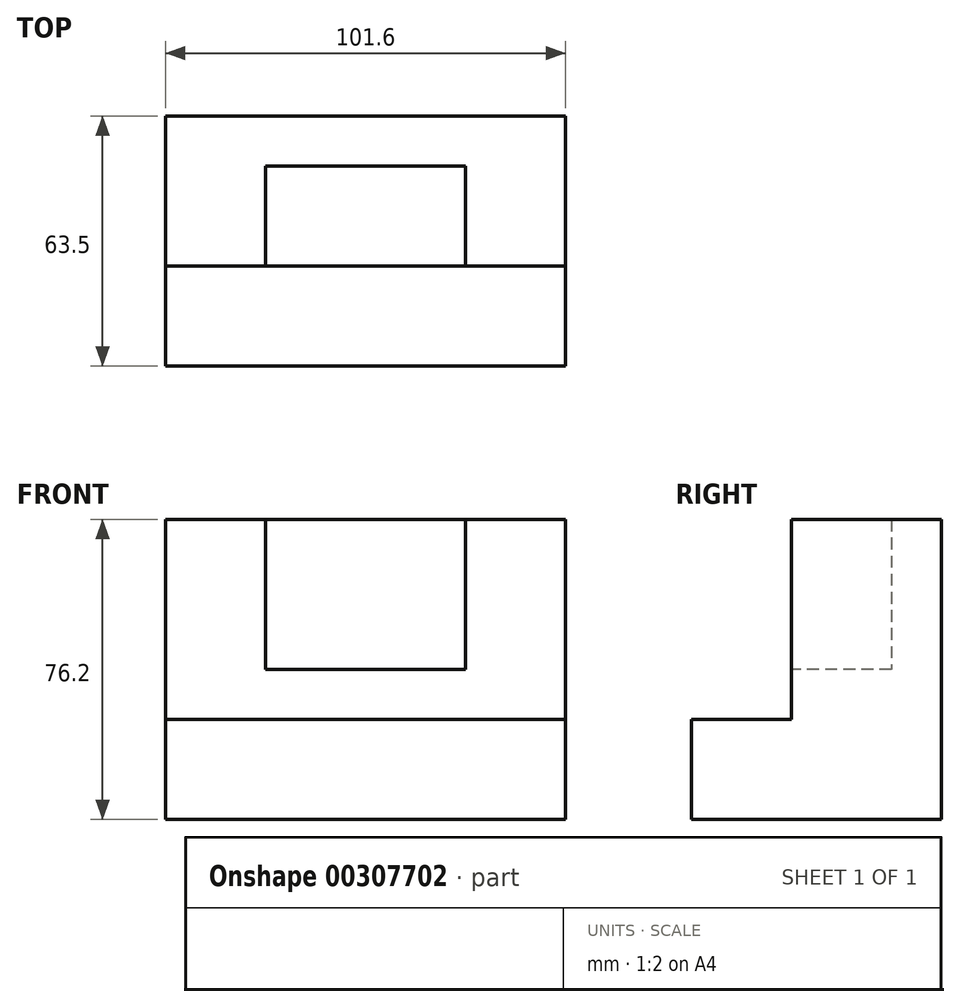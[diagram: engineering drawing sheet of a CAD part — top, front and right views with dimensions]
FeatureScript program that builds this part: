
annotation { "Feature Type Name" : "Feature", "Feature Type Description" : "" }
export const myFeature = defineFeature(function(context is Context, id is Id, definition is map)
    precondition{}
    {
        {
            var Q0;
            Q0=qCreatedBy(makeId("Top.planeOp"),FACE);
            var sketch = newSketch(context, id + "F0", { "sketchPlane" : qUnion([Q0])});
            skLineSegment(sketch, "E0", {"start": v(-56.6, 30.28) * mm, "end": v(45, 30.28) * mm});
            skLineSegment(sketch, "E1", {"start": v(45, 30.28) * mm, "end": v(45, -33.22) * mm});
            skLineSegment(sketch, "E2", {"start": v(45, -33.22) * mm, "end": v(-56.6, -33.22) * mm});
            skLineSegment(sketch, "E3", {"start": v(-56.6, -33.22) * mm, "end": v(-56.6, 30.28) * mm});
            skSolve(sketch);
        }
        {
            var Q0;
            Q0=makeQuery(id+"F0.imprint","IMPRINT",FACE,{"disambiguationData":[TD([[makeQuery(id+"F0.imprint","IMPRINT",EDGE,{"derivedFrom":sQuery(id+"F0.wireOp",EDGE,"E0")}),-1.0]])]});
            extrude(context, id + "F1", {"entities" : qUnion([Q0]), "depth" : 25.4 * mm});
        }
        {
            var Q0;
            Q0=makeQuery(id+"F1.opExtrude","CAP_FACE",FACE,{"disambiguationData":[OSD([sQuery(id+"F0.wireOp",EDGE,"E0"),sQuery(id+"F0.wireOp",EDGE,"E1"),sQuery(id+"F0.wireOp",EDGE,"E2"),sQuery(id+"F0.wireOp",EDGE,"E3")])],"isStart":false});
            var sketch = newSketch(context, id + "F2", { "sketchPlane" : qUnion([Q0])});
            skLineSegment(sketch, "E4", {"start": v(-56.6, -7.82) * mm, "end": v(45, -7.82) * mm});
            skLineSegment(sketch, "E5", {"start": v(45, -7.82) * mm, "end": v(45, 30.28) * mm});
            skLineSegment(sketch, "E6", {"start": v(45, 30.28) * mm, "end": v(-56.6, 30.28) * mm});
            skLineSegment(sketch, "E7", {"start": v(-56.6, 30.28) * mm, "end": v(-56.6, -7.82) * mm});
            skLineSegment(sketch, "E8", {"start": v(-31.2, -7.82) * mm, "end": v(-31.2, 17.58) * mm});
            skLineSegment(sketch, "E9", {"start": v(-31.2, 17.58) * mm, "end": v(19.6, 17.58) * mm});
            skLineSegment(sketch, "E10", {"start": v(19.6, 17.58) * mm, "end": v(19.6, -7.82) * mm});
            skSolve(sketch);
        }
        {
            var Q0;
            {var subQ0=sQuery(id+"F2.wireOp",EDGE,"E5");Q0=makeQuery(id+"F2.imprint","IMPRINT",FACE,{"disambiguationData":[TD([[makeQuery(id+"F2.imprint","IMPRINT",EDGE,{"derivedFrom":subQ0}),-1.0]])]});}
            extrude(context, id + "F3", {"entities" : qUnion([Q0]), "operationType" : NewBodyOperationType.ADD, "depth" : 50.8 * mm});
        }
        {
            var Q0;
            {var subQ0=sQuery(id+"F2.wireOp",EDGE,"E8");Q0=makeQuery(id+"F2.imprint","IMPRINT",FACE,{"disambiguationData":[TD([[makeQuery(id+"F2.imprint","IMPRINT",EDGE,{"derivedFrom":subQ0}),-1.0]])]});}
            extrude(context, id + "F4", {"entities" : qUnion([Q0]), "operationType" : NewBodyOperationType.ADD, "depth" : 12.7 * mm});
        }
    });
